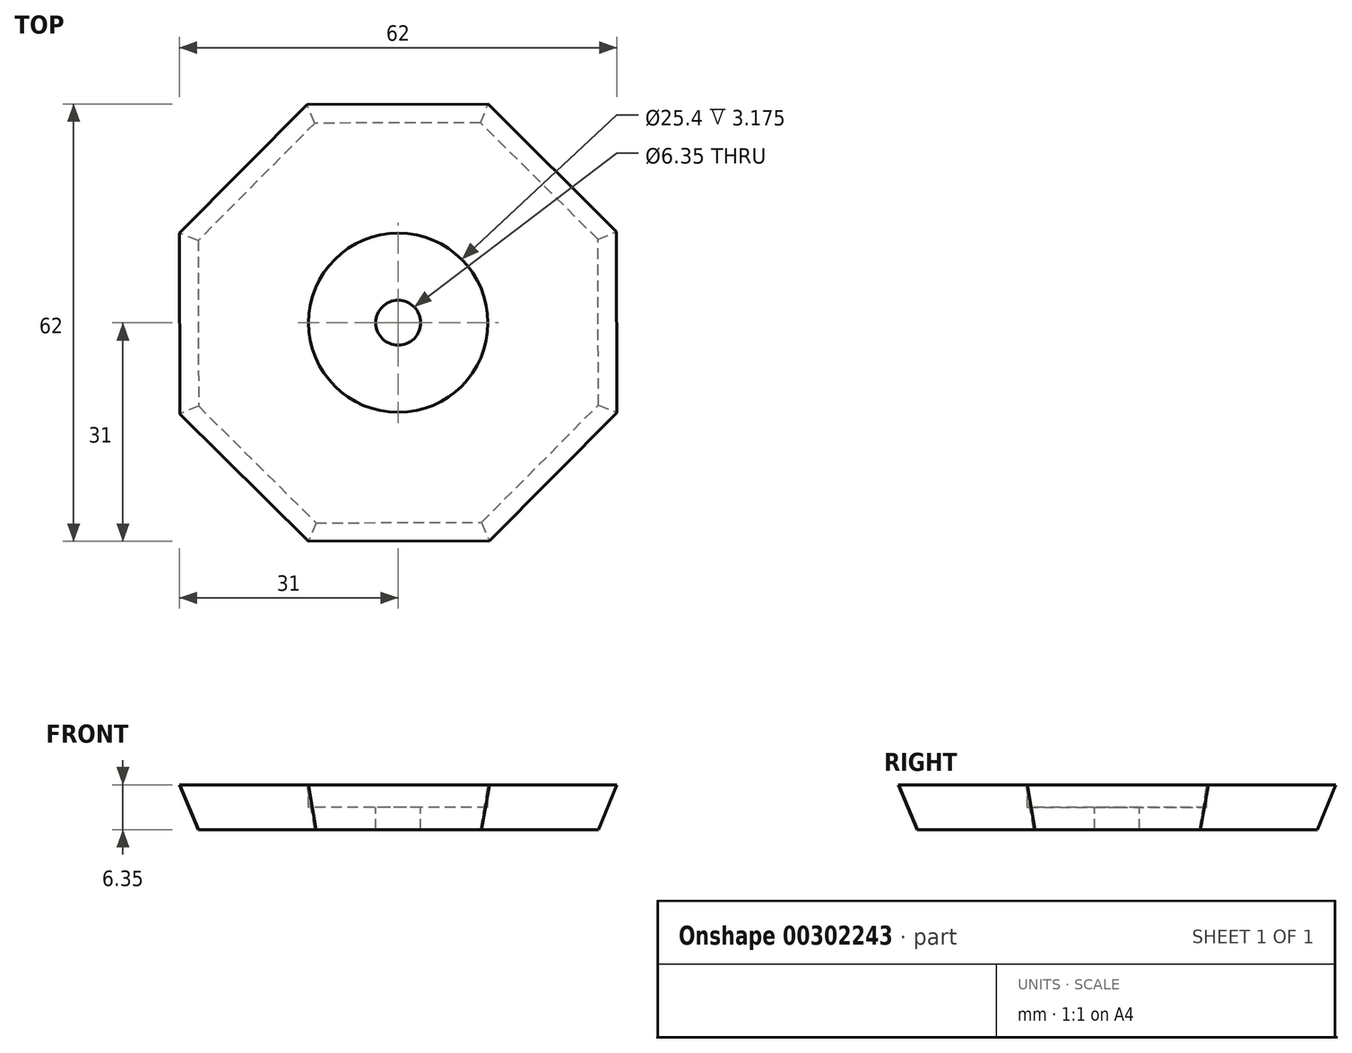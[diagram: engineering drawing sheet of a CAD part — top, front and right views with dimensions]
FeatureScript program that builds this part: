
annotation { "Feature Type Name" : "Feature", "Feature Type Description" : "" }
export const myFeature = defineFeature(function(context is Context, id is Id, definition is map)
    precondition{}
    {
        {
            var Q0;
            Q0=qCreatedBy(makeId("Top.planeOp"),FACE);
            var sketch = newSketch(context, id + "F0", { "sketchPlane" : qUnion([Q0])});
            skCircle(sketch, "E0.cCircle", {"center": v(0, 0) * mm, "radius": 33.5 * mm, "construction": true});
            skLineSegment(sketch, "E0.0", {"start": v(-30.92, -12.92) * mm, "end": v(-31, 12.73) * mm});
            skLineSegment(sketch, "E0.1", {"start": v(-31, 12.73) * mm, "end": v(-12.92, 30.92) * mm});
            skLineSegment(sketch, "E0.2", {"start": v(-12.92, 30.92) * mm, "end": v(12.73, 31) * mm});
            skLineSegment(sketch, "E0.3", {"start": v(12.73, 31) * mm, "end": v(30.92, 12.92) * mm});
            skLineSegment(sketch, "E0.4", {"start": v(30.92, 12.92) * mm, "end": v(31, -12.73) * mm});
            skLineSegment(sketch, "E0.5", {"start": v(31, -12.73) * mm, "end": v(12.92, -30.92) * mm});
            skLineSegment(sketch, "E0.6", {"start": v(12.92, -30.92) * mm, "end": v(-12.73, -31) * mm});
            skLineSegment(sketch, "E0.7", {"start": v(-12.73, -31) * mm, "end": v(-30.92, -12.92) * mm});
            skSolve(sketch);
        }
        {
            var Q0;
            Q0 = qSketchRegion(id + "F0", true);
            extrude(context, id + "F1", {"entities" : qUnion([Q0]), "oppositeDirection" : true, "depth" : 6.35 * mm, "hasDraft" : true, "draftAngle" : 22.5 * degree, "draftPullDirection" : true});
        }
        {
            var Q0;
            Q0=makeQuery(id+"F1.opExtrude","CAP_FACE",FACE,{"disambiguationData":[OSD([sQuery(id+"F0.wireOp",EDGE,"E0.0"),sQuery(id+"F0.wireOp",EDGE,"E0.1"),sQuery(id+"F0.wireOp",EDGE,"E0.2"),sQuery(id+"F0.wireOp",EDGE,"E0.3"),sQuery(id+"F0.wireOp",EDGE,"E0.4"),sQuery(id+"F0.wireOp",EDGE,"E0.5"),sQuery(id+"F0.wireOp",EDGE,"E0.6"),sQuery(id+"F0.wireOp",EDGE,"E0.7")])],"isStart":true});
            var sketch = newSketch(context, id + "F2", { "sketchPlane" : qUnion([Q0])});
            skCircle(sketch, "E1", {"center": v(0, 0) * mm, "radius": 12.7 * mm});
            skSolve(sketch);
        }
        {
            var Q0;
            Q0=makeQuery(id+"F2.imprint","IMPRINT",FACE,{"disambiguationData":[TD([[makeQuery(id+"F2.imprint","IMPRINT",EDGE,{"derivedFrom":sQuery(id+"F2.wireOp",EDGE,"E1")}),1.0]])]});
            extrude(context, id + "F3", {"entities" : qUnion([Q0]), "operationType" : NewBodyOperationType.REMOVE, "oppositeDirection" : true, "depth" : 3.17 * mm});
        }
        {
            var Q0;
            Q0=makeQuery(id+"F3.boolean.opBoolean","COPY",FACE,{"derivedFrom":makeQuery(id+"F3.opExtrude","CAP_FACE",FACE,{"disambiguationData":[OSD([sQuery(id+"F2.wireOp",EDGE,"E1")])],"isStart":false})});
            var sketch = newSketch(context, id + "F4", { "sketchPlane" : qUnion([Q0])});
            skCircle(sketch, "E2", {"center": v(0, 0) * mm, "radius": 3.18 * mm});
            skSolve(sketch);
        }
        {
            var Q0;
            Q0 = qSketchRegion(id + "F4", true);
            extrude(context, id + "F5", {"entities" : qUnion([Q0]), "operationType" : NewBodyOperationType.REMOVE, "oppositeDirection" : true, "depth" : 25.4 * mm});
        }
    });
